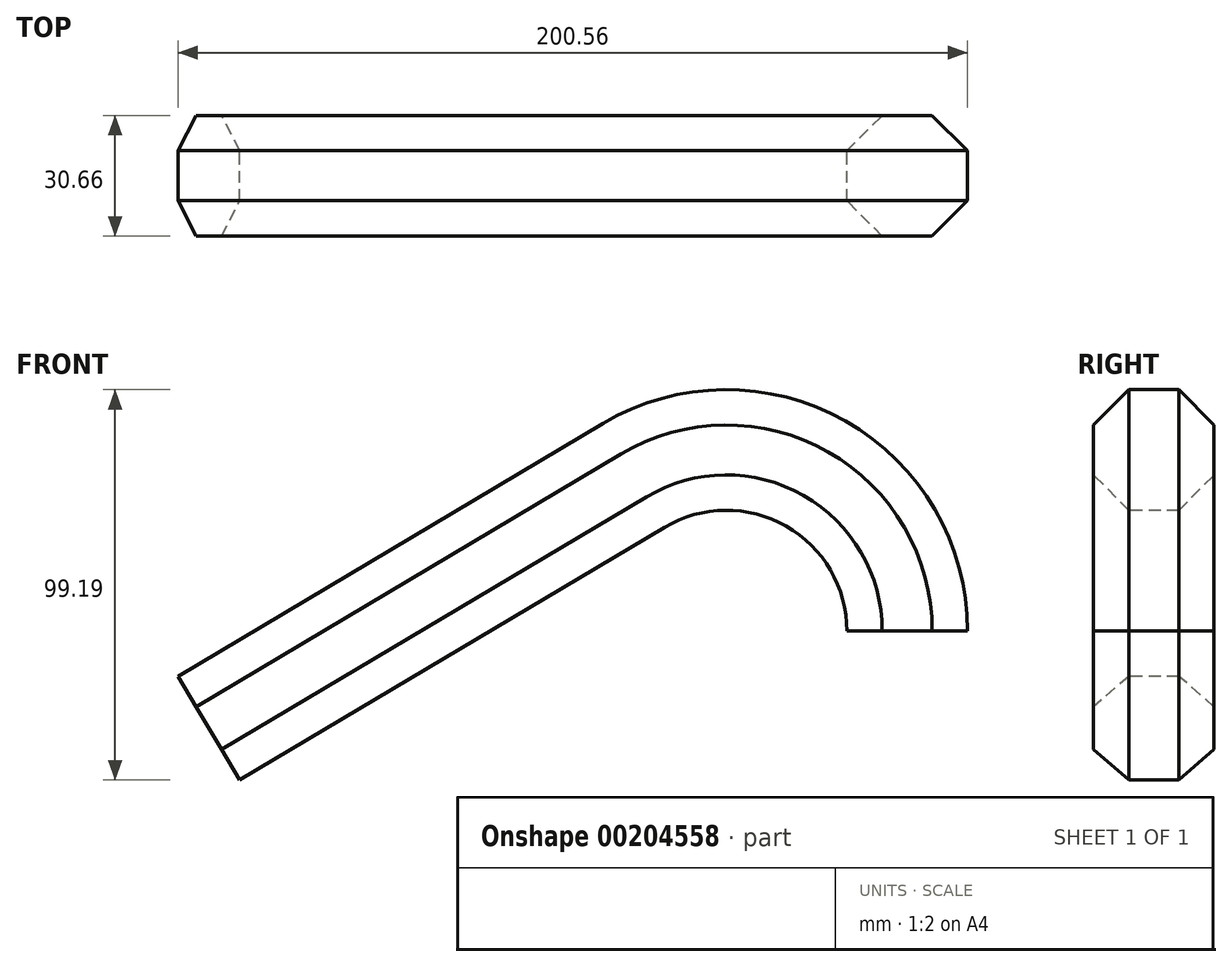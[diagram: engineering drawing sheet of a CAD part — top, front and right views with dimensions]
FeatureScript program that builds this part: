
annotation { "Feature Type Name" : "Feature", "Feature Type Description" : "" }
export const myFeature = defineFeature(function(context is Context, id is Id, definition is map)
    precondition{}
    {
        {
            var Q0;
            Q0=qCreatedBy(makeId("Front.planeOp"),FACE);
            var sketch = newSketch(context, id + "F0", { "sketchPlane" : qUnion([Q0])});
            skArc(sketch, "E0", {"start": v(0, 0) * mm, "mid": v(-8.58, 10.76) * mm, "end": v(-21.32, 15.95) * mm});
            skLineSegment(sketch, "E1", {"start": v(-21.32, 15.95) * mm, "end": v(-71.68, 22.6) * mm});
            skArc(sketch, "E2", {"start": v(-71.68, 22.6) * mm, "mid": v(-89.7, 17.15) * mm, "end": v(-97.47, 0) * mm});
            skLineSegment(sketch, "E3", {"start": v(-97.47, 0) * mm, "end": v(0, 0) * mm, "construction": true});
            skLineSegment(sketch, "E4", {"start": v(-97.47, 0) * mm, "end": v(-97.47, -11.73) * mm});
            skSolve(sketch);
        }
        {
            var Q0;
            Q0=qCreatedBy(makeId("Top.planeOp"),FACE);
            var sketch = newSketch(context, id + "F1", { "sketchPlane" : qUnion([Q0])});
            skCircle(sketch, "E5.cCircle", {"center": v(0, 0) * mm, "radius": 6.86 * mm, "construction": true});
            skLineSegment(sketch, "E5.0", {"start": v(-3.96, 6.86) * mm, "end": v(3.96, 6.86) * mm});
            skLineSegment(sketch, "E5.1", {"start": v(3.96, 6.86) * mm, "end": v(7.92, 0) * mm});
            skLineSegment(sketch, "E5.2", {"start": v(7.92, 0) * mm, "end": v(3.96, -6.86) * mm});
            skLineSegment(sketch, "E5.3", {"start": v(3.96, -6.86) * mm, "end": v(-3.96, -6.86) * mm});
            skLineSegment(sketch, "E5.4", {"start": v(-3.96, -6.86) * mm, "end": v(-7.92, 0) * mm});
            skLineSegment(sketch, "E5.5", {"start": v(-7.92, 0) * mm, "end": v(-3.96, 6.86) * mm});
            skPoint(sketch, "E5.0.midPoint", {"position": v(0, 6.86) * mm});
            skSolve(sketch);
        }
        {
            var Q0;
            Q0=qCreatedBy(makeId("Top.planeOp"),FACE);
            var sketch = newSketch(context, id + "F2", { "sketchPlane" : qUnion([Q0])});
            skLineSegment(sketch, "E6.bottom", {"start": v(-112.7, 17.22) * mm, "end": v(-76.74, 17.22) * mm});
            skLineSegment(sketch, "E6.top", {"start": v(-112.7, -19.96) * mm, "end": v(-76.74, -19.96) * mm});
            skLineSegment(sketch, "E6.left", {"start": v(-112.7, 17.22) * mm, "end": v(-112.7, -19.96) * mm});
            skLineSegment(sketch, "E6.right", {"start": v(-76.74, 17.22) * mm, "end": v(-76.74, -19.96) * mm});
            skSolve(sketch);
        }
        {
            var Q0;
            Q0=qCreatedBy(makeId("Right.planeOp"),FACE);
            var sketch = newSketch(context, id + "F3", { "sketchPlane" : qUnion([Q0])});
            skLineSegment(sketch, "E7.bottom", {"start": v(51.64, 0) * mm, "end": v(64.34, 0) * mm});
            skLineSegment(sketch, "E7.top", {"start": v(51.64, 12.7) * mm, "end": v(64.34, 12.7) * mm});
            skLineSegment(sketch, "E7.left", {"start": v(51.64, 0) * mm, "end": v(51.64, 12.7) * mm});
            skLineSegment(sketch, "E7.right", {"start": v(64.34, 0) * mm, "end": v(64.34, 12.7) * mm});
            skSolve(sketch);
        }
        {
            var Q0;
            Q0=qCreatedBy(makeId("Right.planeOp"),FACE);
            cPlane(context, id + "F4", {"entities" : qUnion([Q0]), "cplaneType" : CPlaneType.OFFSET, "offset" : 25.4 * mm, "oppositeDirection" : true, "width" : 152.4 * mm, "height" : 152.4 * mm});
        }
        {
            var Q0;
            Q0=qCreatedBy(id+"F4.planeOp",FACE);
            var sketch = newSketch(context, id + "F5", { "sketchPlane" : qUnion([Q0])});
            skLineSegment(sketch, "E8.bottom", {"start": v(70.4, -4.94) * mm, "end": v(43.87, -4.94) * mm});
            skLineSegment(sketch, "E8.top", {"start": v(70.4, 21.6) * mm, "end": v(43.87, 21.6) * mm});
            skLineSegment(sketch, "E8.left", {"start": v(70.4, -4.94) * mm, "end": v(70.4, 21.6) * mm});
            skLineSegment(sketch, "E8.right", {"start": v(43.87, -4.94) * mm, "end": v(43.87, 21.6) * mm});
            skSolve(sketch);
        }
        {
            var Q0;
            Q0=qCreatedBy(makeId("Right.planeOp"),FACE);
            cPlane(context, id + "F6", {"entities" : qUnion([Q0]), "cplaneType" : CPlaneType.OFFSET, "offset" : 50.8 * mm, "oppositeDirection" : true, "width" : 152.4 * mm, "height" : 152.4 * mm});
        }
        {
            var Q0;
            Q0=qCreatedBy(id+"F6.planeOp",FACE);
            var sketch = newSketch(context, id + "F7", { "sketchPlane" : qUnion([Q0])});
            skLineSegment(sketch, "E9.bottom", {"start": v(68.74, -2.9) * mm, "end": v(45.94, -2.9) * mm});
            skLineSegment(sketch, "E9.top", {"start": v(68.74, 19.36) * mm, "end": v(45.94, 19.36) * mm});
            skLineSegment(sketch, "E9.left", {"start": v(68.74, -2.9) * mm, "end": v(68.74, 19.36) * mm});
            skLineSegment(sketch, "E9.right", {"start": v(45.94, -2.9) * mm, "end": v(45.94, 19.36) * mm});
            skSolve(sketch);
        }
        {
            var Q0;
            Q0=qCreatedBy(makeId("Right.planeOp"),FACE);
            cPlane(context, id + "F8", {"entities" : qUnion([Q0]), "cplaneType" : CPlaneType.OFFSET, "offset" : 76.2 * mm, "oppositeDirection" : true, "width" : 152.4 * mm, "height" : 152.4 * mm});
        }
        {
            var Q0;
            Q0=qCreatedBy(id+"F8.planeOp",FACE);
            var sketch = newSketch(context, id + "F9", { "sketchPlane" : qUnion([Q0])});
            skLineSegment(sketch, "E10.bottom", {"start": v(69.15, 4.74) * mm, "end": v(39.04, 4.74) * mm});
            skLineSegment(sketch, "E10.top", {"start": v(69.15, 31.64) * mm, "end": v(39.04, 31.64) * mm});
            skLineSegment(sketch, "E10.left", {"start": v(69.15, 4.74) * mm, "end": v(69.15, 31.64) * mm});
            skLineSegment(sketch, "E10.right", {"start": v(39.04, 4.74) * mm, "end": v(39.04, 31.64) * mm});
            skSolve(sketch);
        }
        {
            var Q0;
            Q0=qCreatedBy(makeId("Right.planeOp"),FACE);
            cPlane(context, id + "F10", {"entities" : qUnion([Q0]), "cplaneType" : CPlaneType.OFFSET, "offset" : 101.6 * mm, "oppositeDirection" : true, "width" : 152.4 * mm, "height" : 152.4 * mm});
        }
        {
            var Q0;
            Q0=qCreatedBy(id+"F10.planeOp",FACE);
            var sketch = newSketch(context, id + "F11", { "sketchPlane" : qUnion([Q0])});
            skLineSegment(sketch, "E11.bottom", {"start": v(61.3, 22) * mm, "end": v(51.93, 22) * mm});
            skLineSegment(sketch, "E11.top", {"start": v(61.3, 30.18) * mm, "end": v(51.93, 30.18) * mm});
            skLineSegment(sketch, "E11.left", {"start": v(61.3, 22) * mm, "end": v(61.3, 30.18) * mm});
            skLineSegment(sketch, "E11.right", {"start": v(51.93, 22) * mm, "end": v(51.93, 30.18) * mm});
            skSolve(sketch);
        }
        {
            var Q0;
            Q0=qCreatedBy(makeId("Top.planeOp"),FACE);
            var sketch = newSketch(context, id + "F12", { "sketchPlane" : qUnion([Q0])});
            skLineSegment(sketch, "E12.bottom", {"start": v(-122.43, 62.64) * mm, "end": v(-107.5, 62.64) * mm});
            skLineSegment(sketch, "E12.top", {"start": v(-122.43, 48.31) * mm, "end": v(-107.5, 48.31) * mm});
            skLineSegment(sketch, "E12.left", {"start": v(-122.43, 62.64) * mm, "end": v(-122.43, 48.31) * mm});
            skLineSegment(sketch, "E12.right", {"start": v(-107.5, 62.64) * mm, "end": v(-107.5, 48.31) * mm});
            skSolve(sketch);
        }
        {
            var Q0;
            Q0=qCreatedBy(makeId("Top.planeOp"),FACE);
            var sketch = newSketch(context, id + "F13", { "sketchPlane" : qUnion([Q0])});
            skCircle(sketch, "E13.cCircle", {"center": v(0, 0) * mm, "radius": 15.33 * mm, "construction": true});
            skLineSegment(sketch, "E13.0", {"start": v(-6.35, 15.33) * mm, "end": v(6.35, 15.33) * mm});
            skLineSegment(sketch, "E13.1", {"start": v(6.35, 15.33) * mm, "end": v(15.33, 6.35) * mm});
            skLineSegment(sketch, "E13.2", {"start": v(15.33, 6.35) * mm, "end": v(15.33, -6.35) * mm});
            skLineSegment(sketch, "E13.3", {"start": v(15.33, -6.35) * mm, "end": v(6.35, -15.33) * mm});
            skLineSegment(sketch, "E13.4", {"start": v(6.35, -15.33) * mm, "end": v(-6.35, -15.33) * mm});
            skLineSegment(sketch, "E13.5", {"start": v(-6.35, -15.33) * mm, "end": v(-15.33, -6.35) * mm});
            skLineSegment(sketch, "E13.6", {"start": v(-15.33, -6.35) * mm, "end": v(-15.33, 6.35) * mm});
            skLineSegment(sketch, "E13.7", {"start": v(-15.33, 6.35) * mm, "end": v(-6.35, 15.33) * mm});
            skPoint(sketch, "E13.0.midPoint", {"position": v(0, 15.33) * mm});
            skSolve(sketch);
        }
        {
            var Q0;
            Q0=qCreatedBy(makeId("Front.planeOp"),FACE);
            var sketch = newSketch(context, id + "F14", { "sketchPlane" : qUnion([Q0])});
            skArc(sketch, "E14", {"start": v(0, 0) * mm, "mid": v(-23.23, 39.94) * mm, "end": v(-69.43, 39.48) * mm});
            skLineSegment(sketch, "E15", {"start": v(0, 0) * mm, "end": v(-108.47, 0) * mm, "construction": true});
            skLineSegment(sketch, "E16", {"start": v(-69.43, 39.48) * mm, "end": v(-177.39, -24.74) * mm});
            skSolve(sketch);
        }
        {
            var Q0;
            Q0 = qSketchRegion(id + "F13", true);
            var Q1;
            Q1 = qConstructionFilter(qBodyType(qCreatedBy(id + "F14" ,EDGE), BodyType.WIRE), ConstructionObject.NO);
            sweep(context, id + "F15", {"profiles" : qUnion([Q0]), "path" : qUnion([Q1])});
        }
    });
